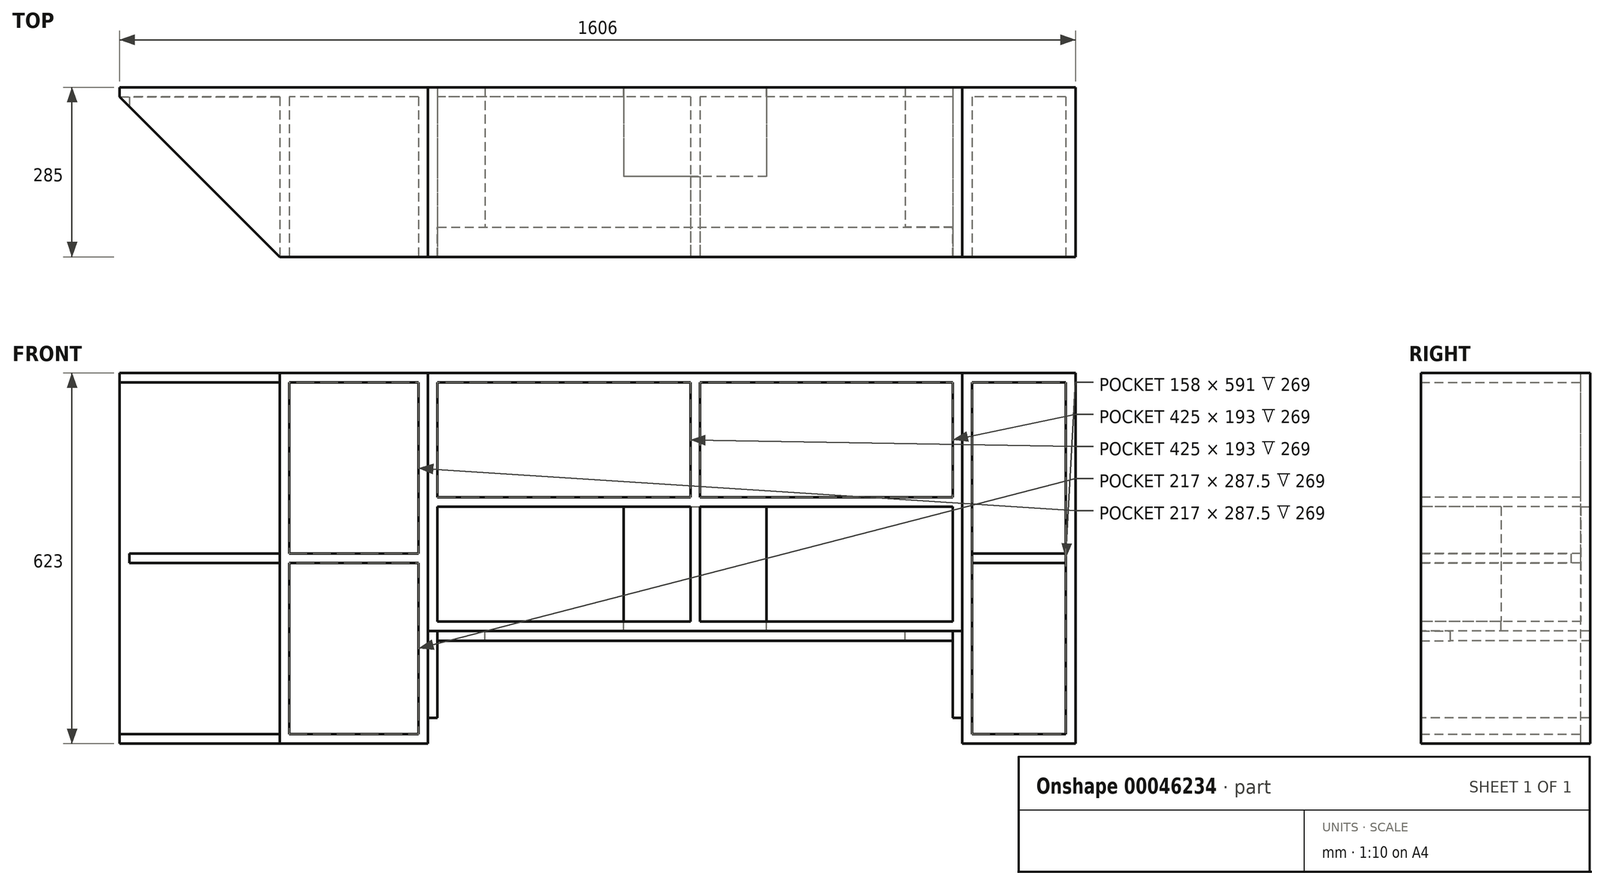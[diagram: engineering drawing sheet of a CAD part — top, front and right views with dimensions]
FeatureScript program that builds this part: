
annotation { "Feature Type Name" : "Feature", "Feature Type Description" : "" }
export const myFeature = defineFeature(function(context is Context, id is Id, definition is map)
    precondition{}
    {
        {
            var Q0;
            Q0=qCreatedBy(makeId("Front.planeOp"),FACE);
            var sketch = newSketch(context, id + "F0", { "sketchPlane" : qUnion([Q0])});
            skLineSegment(sketch, "E0.rect.bottom", {"start": v(-95, -311.5) * mm, "end": v(95, -311.5) * mm});
            skLineSegment(sketch, "E0.rect.top", {"start": v(-95, 311.5) * mm, "end": v(95, 311.5) * mm});
            skLineSegment(sketch, "E0.rect.left", {"start": v(-95, -311.5) * mm, "end": v(-95, 311.5) * mm});
            skLineSegment(sketch, "E0.rect.right", {"start": v(95, -311.5) * mm, "end": v(95, 311.5) * mm});
            skPoint(sketch, "E0.rect.middle", {"position": v(0, 0) * mm});
            skSolve(sketch);
        }
        {
            var Q0;
            Q0 = qSketchRegion(id + "F0", true);
            extrude(context, id + "F1", {"entities" : qUnion([Q0]), "depth" : 285 * mm});
        }
        {
            var Q0;
            Q0=makeQuery(id+"F1.opExtrude","CAP_FACE",FACE,{"disambiguationData":[OSD([sQuery(id+"F0.wireOp",EDGE,"E0.rect.bottom"),sQuery(id+"F0.wireOp",EDGE,"E0.rect.top"),sQuery(id+"F0.wireOp",EDGE,"E0.rect.left"),sQuery(id+"F0.wireOp",EDGE,"E0.rect.right")])],"isStart":false});
            var sketch = newSketch(context, id + "F2", { "sketchPlane" : qUnion([Q0])});
            skLineSegment(sketch, "E1.bottom", {"start": v(-79, -295.5) * mm, "end": v(79, -295.5) * mm});
            skLineSegment(sketch, "E1.top", {"start": v(-79, -8) * mm, "end": v(79, -8) * mm});
            skLineSegment(sketch, "E1.left", {"start": v(-79, -295.5) * mm, "end": v(-79, -8) * mm});
            skLineSegment(sketch, "E1.right", {"start": v(79, -295.5) * mm, "end": v(79, -8) * mm});
            skLineSegment(sketch, "E2.bottom", {"start": v(-79, 295.5) * mm, "end": v(79, 295.5) * mm});
            skLineSegment(sketch, "E2.top", {"start": v(-79, 8) * mm, "end": v(79, 8) * mm});
            skLineSegment(sketch, "E2.left", {"start": v(-79, 295.5) * mm, "end": v(-79, 8) * mm});
            skLineSegment(sketch, "E2.right", {"start": v(79, 295.5) * mm, "end": v(79, 8) * mm});
            skLineSegment(sketch, "E3", {"start": v(0, 0) * mm, "end": v(95, 0) * mm, "construction": true});
            skSolve(sketch);
        }
        {
            var Q0;
            Q0=makeQuery(id+"F1.opExtrude","CAP_FACE",FACE,{"disambiguationData":[OSD([sQuery(id+"F0.wireOp",EDGE,"E0.rect.bottom"),sQuery(id+"F0.wireOp",EDGE,"E0.rect.top"),sQuery(id+"F0.wireOp",EDGE,"E0.rect.left"),sQuery(id+"F0.wireOp",EDGE,"E0.rect.right")])],"isStart":false});
            shell(context, id + "F3", {"entities" : qUnion([Q0]), "thickness" : 16 * mm});
        }
        {
            var Q0;
            Q0=makeQuery(id+"F2.imprint","IMPRINT",FACE,{"disambiguationData":[TD([[makeQuery(id+"F2.imprint","IMPRINT",EDGE,{"derivedFrom":sQuery(id+"F2.wireOp",EDGE,"E1.bottom")}),-1.0]])]});
            var sketch = newSketch(context, id + "F4", { "sketchPlane" : qUnion([Q0])});
            skLineSegment(sketch, "E4.bottom", {"start": v(-79, 8) * mm, "end": v(79, 8) * mm});
            skLineSegment(sketch, "E4.top", {"start": v(-79, -8) * mm, "end": v(79, -8) * mm});
            skLineSegment(sketch, "E4.left", {"start": v(-79, 8) * mm, "end": v(-79, -8) * mm});
            skLineSegment(sketch, "E4.right", {"start": v(79, 8) * mm, "end": v(79, -8) * mm});
            skSolve(sketch);
        }
        {
            var Q0;
            Q0 = qSketchRegion(id + "F4", true);
            var Q1;
            Q1=makeQuery(id+"F3.opShell","OFFSET_FACE",FACE,{"disambiguationData":[OSD([sQuery(id+"F0.wireOp",EDGE,"E0.rect.bottom"),sQuery(id+"F0.wireOp",EDGE,"E0.rect.top"),sQuery(id+"F0.wireOp",EDGE,"E0.rect.left"),sQuery(id+"F0.wireOp",EDGE,"E0.rect.right")])]});
            extrude(context, id + "F5", {"entities" : qUnion([Q0]), "endBound" : BoundingType.UP_TO_SURFACE, "oppositeDirection" : true, "endBoundEntityFace" : qUnion([Q1]), "depth" : 25 * mm});
        }
        {
            var Q0;
            Q0=makeQuery(id+"F2.imprint","IMPRINT",FACE,{"disambiguationData":[TD([[makeQuery(id+"F2.imprint","IMPRINT",EDGE,{"derivedFrom":sQuery(id+"F2.wireOp",EDGE,"E1.bottom")}),-1.0]])]});
            var sketch = newSketch(context, id + "F6", { "sketchPlane" : qUnion([Q0])});
            skLineSegment(sketch, "E5.bottom", {"start": v(-95, 311.5) * mm, "end": v(-993, 311.5) * mm});
            skLineSegment(sketch, "E5.top", {"start": v(-95, -122.5) * mm, "end": v(-993, -122.5) * mm});
            skLineSegment(sketch, "E5.left", {"start": v(-95, 311.5) * mm, "end": v(-95, -122.5) * mm});
            skLineSegment(sketch, "E5.right", {"start": v(-993, 311.5) * mm, "end": v(-993, -122.5) * mm});
            skSolve(sketch);
        }
        {
            var Q0;
            Q0 = qSketchRegion(id + "F6", true);
            extrude(context, id + "F7", {"entities" : qUnion([Q0]), "oppositeDirection" : true, "depth" : 285 * mm});
        }
        {
            var Q0;
            Q0=makeQuery(id+"F7.opExtrude","CAP_FACE",FACE,{"disambiguationData":[OSD([sQuery(id+"F6.wireOp",EDGE,"E5.bottom"),sQuery(id+"F6.wireOp",EDGE,"E5.top"),sQuery(id+"F6.wireOp",EDGE,"E5.left"),sQuery(id+"F6.wireOp",EDGE,"E5.right")])],"isStart":true});
            shell(context, id + "F8", {"entities" : qUnion([Q0]), "thickness" : 16 * mm});
        }
        {
            var Q0;
            Q0=makeQuery(id+"F7.opExtrude","CAP_FACE",FACE,{"disambiguationData":[OSD([sQuery(id+"F6.wireOp",EDGE,"E5.bottom"),sQuery(id+"F6.wireOp",EDGE,"E5.top"),sQuery(id+"F6.wireOp",EDGE,"E5.left"),sQuery(id+"F6.wireOp",EDGE,"E5.right")])],"isStart":true});
            var sketch = newSketch(context, id + "F9", { "sketchPlane" : qUnion([Q0])});
            skLineSegment(sketch, "E6.bottom", {"start": v(-552, 295.5) * mm, "end": v(-536, 295.5) * mm});
            skLineSegment(sketch, "E6.top", {"start": v(-552, -106.5) * mm, "end": v(-536, -106.5) * mm});
            skLineSegment(sketch, "E6.left", {"start": v(-552, 295.5) * mm, "end": v(-552, -106.5) * mm});
            skLineSegment(sketch, "E6.right", {"start": v(-536, 295.5) * mm, "end": v(-536, -106.5) * mm});
            skLineSegment(sketch, "E7", {"start": v(-544, 311.5) * mm, "end": v(-544, 122.9) * mm, "construction": true});
            skPoint(sketch, "E7.endSnap0", {"position": v(-544, 311.5) * mm});
            skSolve(sketch);
        }
        {
            var Q0;
            Q0 = qSketchRegion(id + "F9", true);
            var Q1;
            Q1=makeQuery(id+"F8.opShell","OFFSET_FACE",FACE,{"disambiguationData":[OSD([sQuery(id+"F6.wireOp",EDGE,"E5.bottom"),sQuery(id+"F6.wireOp",EDGE,"E5.top"),sQuery(id+"F6.wireOp",EDGE,"E5.left"),sQuery(id+"F6.wireOp",EDGE,"E5.right")])]});
            extrude(context, id + "F10", {"entities" : qUnion([Q0]), "endBound" : BoundingType.UP_TO_SURFACE, "oppositeDirection" : true, "endBoundEntityFace" : qUnion([Q1]), "depth" : 25 * mm});
        }
        {
            var Q0;
            Q0=makeQuery(id+"F7.opExtrude","CAP_FACE",FACE,{"disambiguationData":[OSD([sQuery(id+"F6.wireOp",EDGE,"E5.bottom"),sQuery(id+"F6.wireOp",EDGE,"E5.top"),sQuery(id+"F6.wireOp",EDGE,"E5.left"),sQuery(id+"F6.wireOp",EDGE,"E5.right")])],"isStart":true});
            var sketch = newSketch(context, id + "F11", { "sketchPlane" : qUnion([Q0])});
            skLineSegment(sketch, "E8.bottom", {"start": v(-977, 102.5) * mm, "end": v(-111, 102.5) * mm});
            skLineSegment(sketch, "E8.top", {"start": v(-977, 86.5) * mm, "end": v(-111, 86.5) * mm});
            skLineSegment(sketch, "E8.left", {"start": v(-977, 102.5) * mm, "end": v(-977, 86.5) * mm});
            skLineSegment(sketch, "E8.right", {"start": v(-111, 102.5) * mm, "end": v(-111, 86.5) * mm});
            skLineSegment(sketch, "E9", {"start": v(-993, 94.5) * mm, "end": v(-845.97, 94.5) * mm});
            skSolve(sketch);
        }
        {
            var Q0;
            Q0 = qSketchRegion(id + "F11", true);
            var Q1;
            Q1=makeQuery(id+"F8.opShell","OFFSET_FACE",FACE,{"disambiguationData":[OSD([sQuery(id+"F6.wireOp",EDGE,"E5.bottom"),sQuery(id+"F6.wireOp",EDGE,"E5.top"),sQuery(id+"F6.wireOp",EDGE,"E5.left"),sQuery(id+"F6.wireOp",EDGE,"E5.right")])]});
            extrude(context, id + "F12", {"entities" : qUnion([Q0]), "operationType" : NewBodyOperationType.ADD, "endBound" : BoundingType.UP_TO_SURFACE, "oppositeDirection" : true, "endBoundEntityFace" : qUnion([Q1]), "depth" : 25 * mm});
        }
        {
            var Q0;
            Q0=makeQuery(id+"F7.opExtrude","CAP_FACE",FACE,{"disambiguationData":[OSD([sQuery(id+"F6.wireOp",EDGE,"E5.bottom"),sQuery(id+"F6.wireOp",EDGE,"E5.top"),sQuery(id+"F6.wireOp",EDGE,"E5.left"),sQuery(id+"F6.wireOp",EDGE,"E5.right")])],"isStart":true});
            var sketch = newSketch(context, id + "F13", { "sketchPlane" : qUnion([Q0])});
            skLineSegment(sketch, "E10.bottom", {"start": v(-993, 311.5) * mm, "end": v(-1511, 311.5) * mm});
            skLineSegment(sketch, "E10.top", {"start": v(-993, -311.5) * mm, "end": v(-1511, -311.5) * mm});
            skLineSegment(sketch, "E10.left", {"start": v(-993, 311.5) * mm, "end": v(-993, -311.5) * mm});
            skLineSegment(sketch, "E10.right", {"start": v(-1511, 311.5) * mm, "end": v(-1511, -311.5) * mm});
            skSolve(sketch);
        }
        {
            var Q0;
            Q0 = qSketchRegion(id + "F13", true);
            var Q1;
            Q1=makeQuery(id+"F7.opExtrude","CAP_FACE",FACE,{"disambiguationData":[OSD([sQuery(id+"F6.wireOp",EDGE,"E5.bottom"),sQuery(id+"F6.wireOp",EDGE,"E5.top"),sQuery(id+"F6.wireOp",EDGE,"E5.left"),sQuery(id+"F6.wireOp",EDGE,"E5.right")])],"isStart":false});
            extrude(context, id + "F14", {"entities" : qUnion([Q0]), "endBound" : BoundingType.UP_TO_SURFACE, "oppositeDirection" : true, "endBoundEntityFace" : qUnion([Q1]), "depth" : 25 * mm});
        }
        {
            var Q0;
            Q0=makeQuery(id+"F14.opExtrude","CAP_FACE",FACE,{"disambiguationData":[OSD([sQuery(id+"F13.wireOp",EDGE,"E10.bottom"),sQuery(id+"F13.wireOp",EDGE,"E10.top"),sQuery(id+"F13.wireOp",EDGE,"E10.left"),sQuery(id+"F13.wireOp",EDGE,"E10.right")])],"isStart":true});
            shell(context, id + "F15", {"entities" : qUnion([Q0]), "thickness" : 16 * mm});
        }
        {
            var Q0;
            Q0=makeQuery(id+"F14.opExtrude","SWEPT_FACE",FACE,{"disambiguationData":[OSD([sQuery(id+"F13.wireOp",EDGE,"E10.bottom")])]});
            var sketch = newSketch(context, id + "F16", { "sketchPlane" : qUnion([Q0])});
            skLineSegment(sketch, "E11", {"start": v(-1511, -16) * mm, "end": v(-1242, -285) * mm});
            skSolve(sketch);
        }
        {
            var Q0;
            Q0=makeQuery(id+"F14.opExtrude","CAP_FACE",FACE,{"disambiguationData":[OSD([sQuery(id+"F13.wireOp",EDGE,"E10.bottom"),sQuery(id+"F13.wireOp",EDGE,"E10.top"),sQuery(id+"F13.wireOp",EDGE,"E10.left"),sQuery(id+"F13.wireOp",EDGE,"E10.right")])],"isStart":true});
            var sketch = newSketch(context, id + "F17", { "sketchPlane" : qUnion([Q0])});
            skLineSegment(sketch, "E12.bottom", {"start": v(-1242, 295.5) * mm, "end": v(-1226, 295.5) * mm});
            skLineSegment(sketch, "E12.top", {"start": v(-1242, -295.5) * mm, "end": v(-1226, -295.5) * mm});
            skLineSegment(sketch, "E12.left", {"start": v(-1242, 295.5) * mm, "end": v(-1242, -295.5) * mm});
            skLineSegment(sketch, "E12.right", {"start": v(-1226, 295.5) * mm, "end": v(-1226, -295.5) * mm});
            skSolve(sketch);
        }
        {
            var Q0;
            Q0 = qSketchRegion(id + "F17", true);
            var Q1;
            Q1=makeQuery(id+"F15.opShell","OFFSET_FACE",FACE,{"disambiguationData":[OSD([sQuery(id+"F13.wireOp",EDGE,"E10.bottom"),sQuery(id+"F13.wireOp",EDGE,"E10.top"),sQuery(id+"F13.wireOp",EDGE,"E10.left"),sQuery(id+"F13.wireOp",EDGE,"E10.right")])]});
            extrude(context, id + "F18", {"entities" : qUnion([Q0]), "endBound" : BoundingType.UP_TO_SURFACE, "oppositeDirection" : true, "endBoundEntityFace" : qUnion([Q1]), "depth" : 25 * mm});
        }
        {
            var Q0;
            Q0=makeQuery(id+"F14.opExtrude","CAP_FACE",FACE,{"disambiguationData":[OSD([sQuery(id+"F13.wireOp",EDGE,"E10.bottom"),sQuery(id+"F13.wireOp",EDGE,"E10.top"),sQuery(id+"F13.wireOp",EDGE,"E10.left"),sQuery(id+"F13.wireOp",EDGE,"E10.right")])],"isStart":true});
            var sketch = newSketch(context, id + "F19", { "sketchPlane" : qUnion([Q0])});
            skLineSegment(sketch, "E13.bottom", {"start": v(-1511, 8) * mm, "end": v(-1009, 8) * mm});
            skLineSegment(sketch, "E13.top", {"start": v(-1511, -8) * mm, "end": v(-1009, -8) * mm});
            skLineSegment(sketch, "E13.left", {"start": v(-1511, 8) * mm, "end": v(-1511, -8) * mm});
            skLineSegment(sketch, "E13.right", {"start": v(-1009, 8) * mm, "end": v(-1009, -8) * mm});
            skLineSegment(sketch, "E14", {"start": v(-1511, 0) * mm, "end": v(-1429.09, 0) * mm, "construction": true});
            skPoint(sketch, "E14.endSnap0", {"position": v(-1511, 0) * mm});
            skSolve(sketch);
        }
        {
            var Q0;
            Q0 = qSketchRegion(id + "F19", true);
            var Q1;
            Q1=makeQuery(id+"F15.opShell","OFFSET_FACE",FACE,{"disambiguationData":[OSD([sQuery(id+"F13.wireOp",EDGE,"E10.bottom"),sQuery(id+"F13.wireOp",EDGE,"E10.top"),sQuery(id+"F13.wireOp",EDGE,"E10.left"),sQuery(id+"F13.wireOp",EDGE,"E10.right")])]});
            extrude(context, id + "F20", {"entities" : qUnion([Q0]), "operationType" : NewBodyOperationType.ADD, "endBound" : BoundingType.UP_TO_SURFACE, "oppositeDirection" : true, "endBoundEntityFace" : qUnion([Q1]), "depth" : 25 * mm});
        }
        {
            var Q0;
            Q0=makeQuery(id+"F14.opExtrude","CAP_FACE",FACE,{"disambiguationData":[OSD([sQuery(id+"F13.wireOp",EDGE,"E10.bottom"),sQuery(id+"F13.wireOp",EDGE,"E10.top"),sQuery(id+"F13.wireOp",EDGE,"E10.left"),sQuery(id+"F13.wireOp",EDGE,"E10.right")])],"isStart":true});
            var sketch = newSketch(context, id + "F21", { "sketchPlane" : qUnion([Q0])});
            skLineSegment(sketch, "E15.bottom", {"start": v(-1495, 295.5) * mm, "end": v(-1511, 295.5) * mm});
            skLineSegment(sketch, "E15.top", {"start": v(-1495, -295.5) * mm, "end": v(-1511, -295.5) * mm});
            skLineSegment(sketch, "E15.left", {"start": v(-1495, 295.5) * mm, "end": v(-1495, -295.5) * mm});
            skLineSegment(sketch, "E15.right", {"start": v(-1511, 295.5) * mm, "end": v(-1511, -295.5) * mm});
            skSolve(sketch);
        }
        {
            var Q0;
            Q0 = qSketchRegion(id + "F21", true);
            var Q1;
            Q1=makeQuery(id+"F15.opShell","OFFSET_FACE",FACE,{"disambiguationData":[OSD([sQuery(id+"F13.wireOp",EDGE,"E10.bottom"),sQuery(id+"F13.wireOp",EDGE,"E10.top"),sQuery(id+"F13.wireOp",EDGE,"E10.left"),sQuery(id+"F13.wireOp",EDGE,"E10.right")])]});
            extrude(context, id + "F22", {"entities" : qUnion([Q0]), "operationType" : NewBodyOperationType.REMOVE, "endBound" : BoundingType.UP_TO_SURFACE, "oppositeDirection" : true, "endBoundEntityFace" : qUnion([Q1]), "depth" : 25 * mm});
        }
        {
            var Q0;
            {var subQ2=sQuery(id+"F16.wireOp",EDGE,"E11");Q0=makeQuery(id+"F16.imprint","IMPRINT",FACE,{"disambiguationData":[TD([[makeQuery(id+"F16.imprint","IMPRINT",EDGE,{"derivedFrom":subQ2}),-1.0]])]});}
            extrude(context, id + "F23", {"entities" : qUnion([Q0]), "operationType" : NewBodyOperationType.REMOVE, "endBound" : BoundingType.THROUGH_ALL, "oppositeDirection" : true, "depth" : 25 * mm});
        }
        {
            var Q0;
            Q0=makeQuery(id+"F14.opExtrude","SWEPT_FACE",FACE,{"disambiguationData":[OSD([sQuery(id+"F13.wireOp",EDGE,"E10.left")])]});
            var sketch = newSketch(context, id + "F24", { "sketchPlane" : qUnion([Q0])});
            skLineSegment(sketch, "E16.bottom", {"start": v(0, -268.5) * mm, "end": v(-285, -268.5) * mm});
            skLineSegment(sketch, "E16.top", {"start": v(0, -122.5) * mm, "end": v(-285, -122.5) * mm});
            skLineSegment(sketch, "E16.left", {"start": v(0, -268.5) * mm, "end": v(0, -122.5) * mm});
            skLineSegment(sketch, "E16.right", {"start": v(-285, -268.5) * mm, "end": v(-285, -122.5) * mm});
            skSolve(sketch);
        }
        {
            var Q0;
            Q0 = qSketchRegion(id + "F24", true);
            extrude(context, id + "F25", {"entities" : qUnion([Q0]), "depth" : 16 * mm});
        }
        {
            var Q0;
            Q0=makeQuery(id+"F1.opExtrude","SWEPT_FACE",FACE,{"disambiguationData":[OSD([sQuery(id+"F0.wireOp",EDGE,"E0.rect.left")])]});
            var sketch = newSketch(context, id + "F26", { "sketchPlane" : qUnion([Q0])});
            skLineSegment(sketch, "E17.bottom", {"start": v(0, -268.5) * mm, "end": v(285, -268.5) * mm});
            skLineSegment(sketch, "E17.top", {"start": v(0, -122.5) * mm, "end": v(285, -122.5) * mm});
            skLineSegment(sketch, "E17.left", {"start": v(0, -268.5) * mm, "end": v(0, -122.5) * mm});
            skLineSegment(sketch, "E17.right", {"start": v(285, -268.5) * mm, "end": v(285, -122.5) * mm});
            skSolve(sketch);
        }
        {
            var Q0;
            Q0 = qSketchRegion(id + "F26", true);
            extrude(context, id + "F27", {"entities" : qUnion([Q0]), "depth" : 16 * mm});
        }
        {
            var Q0;
            Q0=makeQuery(id+"F7.opExtrude","CAP_FACE",FACE,{"disambiguationData":[OSD([sQuery(id+"F6.wireOp",EDGE,"E5.bottom"),sQuery(id+"F6.wireOp",EDGE,"E5.top"),sQuery(id+"F6.wireOp",EDGE,"E5.left"),sQuery(id+"F6.wireOp",EDGE,"E5.right")])],"isStart":false});
            var sketch = newSketch(context, id + "F28", { "sketchPlane" : qUnion([Q0])});
            skLineSegment(sketch, "E18.rect.bottom", {"start": v(664, -331.5) * mm, "end": v(424, -331.5) * mm});
            skLineSegment(sketch, "E18.rect.top", {"start": v(664, 86.5) * mm, "end": v(424, 86.5) * mm});
            skLineSegment(sketch, "E18.rect.left", {"start": v(664, -331.5) * mm, "end": v(664, 86.5) * mm});
            skLineSegment(sketch, "E18.rect.right", {"start": v(424, -331.5) * mm, "end": v(424, 86.5) * mm});
            skPoint(sketch, "E18.rect.middle", {"position": v(544, -122.5) * mm});
            skSolve(sketch);
        }
        {
            var Q0;
            Q0 = qSketchRegion(id + "F28", true);
            extrude(context, id + "F29", {"entities" : qUnion([Q0]), "operationType" : NewBodyOperationType.REMOVE, "oppositeDirection" : true, "depth" : 150 * mm});
        }
        {
            var Q0;
            Q0=makeQuery(id+"F7.opExtrude","SWEPT_FACE",FACE,{"disambiguationData":[OSD([sQuery(id+"F6.wireOp",EDGE,"E5.top")])]});
            var sketch = newSketch(context, id + "F30", { "sketchPlane" : qUnion([Q0])});
            skSolve(sketch);
        }
        {
            var Q0;
            {var subQ0=sQuery(id+"F6.wireOp",EDGE,"E5.top");Q0=makeQuery(id+"F30.imprint","IMPRINT",FACE,{"disambiguationData":[TD([[makeQuery(id+"F30.imprint","IMPRINT",EDGE,{"derivedFrom":makeQuery(id+"F7.opExtrude","CAP_EDGE",EDGE,{"disambiguationData":[OSD([subQ0])],"isStart":true})}),1.0]])]});}
            var sketch = newSketch(context, id + "F31", { "sketchPlane" : qUnion([Q0])});
            skLineSegment(sketch, "E19.bottom", {"start": v(-977, 285) * mm, "end": v(-111, 285) * mm});
            skLineSegment(sketch, "E19.top", {"start": v(-977, 235) * mm, "end": v(-111, 235) * mm});
            skLineSegment(sketch, "E19.left", {"start": v(-977, 285) * mm, "end": v(-977, 235) * mm});
            skLineSegment(sketch, "E19.right", {"start": v(-111, 285) * mm, "end": v(-111, 235) * mm});
            skSolve(sketch);
        }
        {
            var Q0;
            Q0 = qSketchRegion(id + "F31", true);
            extrude(context, id + "F32", {"entities" : qUnion([Q0]), "depth" : 16 * mm});
        }
        {
            var Q0;
            {var subQ0=sQuery(id+"F6.wireOp",EDGE,"E5.top");Q0=makeQuery(id+"F30.imprint","IMPRINT",FACE,{"disambiguationData":[TD([[makeQuery(id+"F30.imprint","IMPRINT",EDGE,{"derivedFrom":makeQuery(id+"F7.opExtrude","CAP_EDGE",EDGE,{"disambiguationData":[OSD([subQ0])],"isStart":true})}),1.0]])]});}
            var sketch = newSketch(context, id + "F33", { "sketchPlane" : qUnion([Q0])});
            skLineSegment(sketch, "E20.bottom", {"start": v(-977, 0) * mm, "end": v(-897, 0) * mm});
            skLineSegment(sketch, "E20.top", {"start": v(-977, 235) * mm, "end": v(-897, 235) * mm});
            skLineSegment(sketch, "E20.left", {"start": v(-977, 0) * mm, "end": v(-977, 235) * mm});
            skLineSegment(sketch, "E20.right", {"start": v(-897, 0) * mm, "end": v(-897, 235) * mm});
            skLineSegment(sketch, "E21.bottom", {"start": v(-111, 0) * mm, "end": v(-191, 0) * mm});
            skLineSegment(sketch, "E21.top", {"start": v(-111, 235) * mm, "end": v(-191, 235) * mm});
            skLineSegment(sketch, "E21.left", {"start": v(-111, 0) * mm, "end": v(-111, 235) * mm});
            skLineSegment(sketch, "E21.right", {"start": v(-191, 0) * mm, "end": v(-191, 235) * mm});
            skSolve(sketch);
        }
        {
            var Q0;
            Q0 = qSketchRegion(id + "F33", true);
            extrude(context, id + "F34", {"entities" : qUnion([Q0]), "depth" : 16 * mm});
        }
    });
